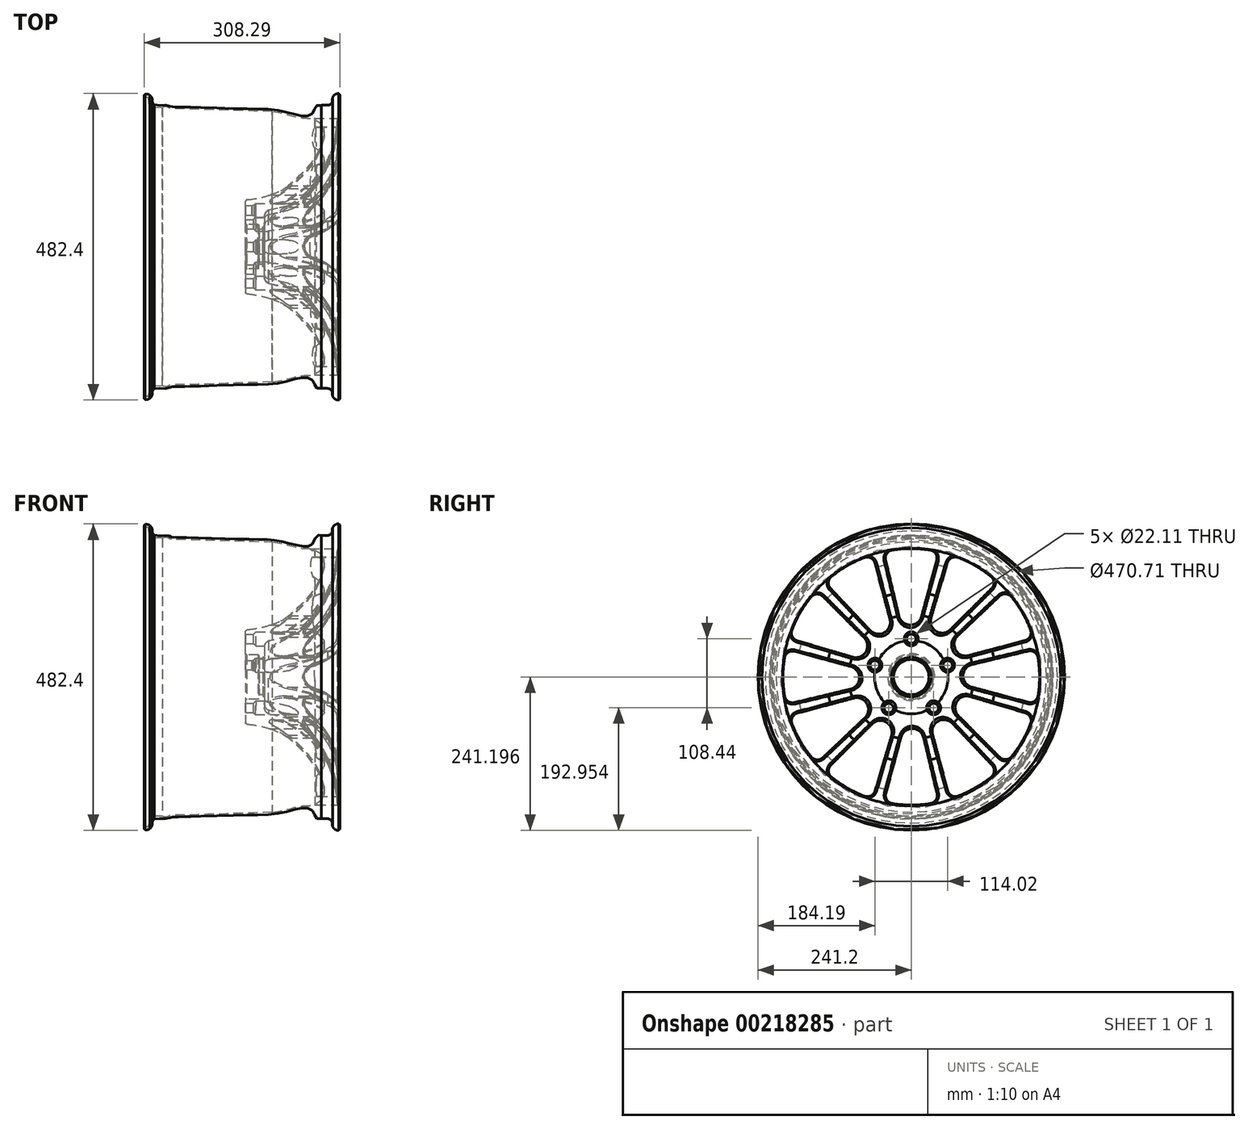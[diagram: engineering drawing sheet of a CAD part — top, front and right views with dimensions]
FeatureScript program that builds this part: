
annotation { "Feature Type Name" : "Feature", "Feature Type Description" : "" }
export const myFeature = defineFeature(function(context is Context, id is Id, definition is map)
    precondition{}
    {
        {
            var Q0;
            Q0=qCreatedBy(makeId("Front.planeOp"),FACE);
            var sketch = newSketch(context, id + "F0", { "sketchPlane" : qUnion([Q0])});
            skLineSegment(sketch, "E0", {"start": v(-76.45, -36.51) * mm, "end": v(-76.45, -20.16) * mm});
            skLineSegment(sketch, "E1", {"start": v(-69.98, -9.89) * mm, "end": v(-37.23, -2.41) * mm});
            skArc(sketch, "E2", {"start": v(-69.98, -9.89) * mm, "mid": v(-74.7, -14.09) * mm, "end": v(-76.45, -20.16) * mm});
            skFitSpline(sketch, "E3", {"points": [v(-37.23, -2.41) * mm, v(-17.73, 6.45) * mm, v(2.3, 30.38) * mm], "startDerivative": vector(46.63, 15.97) * mm, "endDerivative": vector(34.44, 46.87) * mm});
            skFitSpline(sketch, "E4", {"points": [v(2.3, 30.38) * mm, v(23.11, 65.83) * mm], "startDerivative": vector(28.94, 36.21) * mm, "endDerivative": vector(17.75, 37.52) * mm});
            skFitSpline(sketch, "E5", {"points": [v(23.11, 65.83) * mm, v(40.09, 126.8) * mm, v(40.76, 134.95) * mm], "startDerivative": vector(48.73, 100.19) * mm, "endDerivative": vector(-0.18, 23.94) * mm});
            skFitSpline(sketch, "E6", {"points": [v(40.76, 134.95) * mm, v(40.76, 158.65) * mm, v(41.73, 167.17) * mm], "startDerivative": vector(2.63, 42.3) * mm, "endDerivative": vector(3.15, 18.57) * mm});
            skArc(sketch, "E7", {"start": v(41.73, 167.17) * mm, "mid": v(42.53, 170.69) * mm, "end": v(40.17, 173.42) * mm});
            skArc(sketch, "E8", {"start": v(40.17, 173.42) * mm, "mid": v(34.51, 171.85) * mm, "end": v(30.96, 167.17) * mm});
            skFitSpline(sketch, "E9", {"points": [v(30.96, 167.17) * mm, v(30.02, 160.2) * mm, v(25.65, 155.75) * mm, v(12.9, 154.85) * mm], "startDerivative": vector(-11.18, -23.98) * mm, "endDerivative": vector(-39.84, -5.43) * mm});
            skFitSpline(sketch, "E10", {"points": [v(12.9, 154.85) * mm, v(10.67, 155.98) * mm, v(5.92, 154.3) * mm, v(-2.23, 140.57) * mm, v(-9.2, 138.22) * mm, v(-18.92, 138.56) * mm, v(-41.3, 143.92) * mm, v(-63.75, 148.22) * mm, v(-89.43, 149.11) * mm, v(-144.26, 150.4) * mm, v(-204.89, 152.18) * mm, v(-223.48, 152.85) * mm, v(-225.49, 153.97) * mm, v(-228.56, 155.48) * mm, v(-236.43, 154.85) * mm, v(-249.44, 155.76) * mm], "startDerivative": vector(-71.66, 50.77) * mm, "endDerivative": vector(-216.1, 28.33) * mm});
            skArc(sketch, "E11", {"start": v(-252.9, 162.18) * mm, "mid": v(-252.1, 158.47) * mm, "end": v(-249.44, 155.76) * mm});
            skArc(sketch, "E12", {"start": v(-252.9, 162.18) * mm, "mid": v(-253.67, 167) * mm, "end": v(-256.75, 170.77) * mm});
            skArc(sketch, "E13", {"start": v(-256.75, 170.77) * mm, "mid": v(-260.2, 172.5) * mm, "end": v(-264.07, 172.45) * mm});
            skArc(sketch, "E14", {"start": v(-264.07, 172.45) * mm, "mid": v(-265.64, 170.02) * mm, "end": v(-264.07, 167.6) * mm});
            skLineSegment(sketch, "E15", {"start": v(-264.07, 167.6) * mm, "end": v(-260.33, 167.6) * mm});
            skArc(sketch, "E16", {"start": v(-258.37, 165.7) * mm, "mid": v(-258.96, 167.04) * mm, "end": v(-260.33, 167.6) * mm});
            skLineSegment(sketch, "E17", {"start": v(-258.37, 165.7) * mm, "end": v(-258.2, 160.06) * mm});
            skArc(sketch, "E18", {"start": v(-258.2, 160.06) * mm, "mid": v(-255.87, 154.31) * mm, "end": v(-250.33, 151.51) * mm});
            skLineSegment(sketch, "E19", {"start": v(-250.33, 151.51) * mm, "end": v(-237.32, 151.07) * mm});
            skFitSpline(sketch, "E20", {"points": [v(-237.32, 151.07) * mm, v(-230.51, 152.52) * mm, v(-225.15, 150.12) * mm, v(-217.28, 149.5) * mm, v(-64.03, 144.98) * mm], "startDerivative": vector(53.95, 20.8) * mm, "endDerivative": vector(330.22, -11.39) * mm});
            skFitSpline(sketch, "E21", {"points": [v(-64.03, 144.98) * mm, v(-23.16, 135.94) * mm, v(-8.6, 134.65) * mm, v(2.9, 134.04) * mm], "startDerivative": vector(115.17, -13.47) * mm, "endDerivative": vector(46.54, -2.62) * mm});
            skArc(sketch, "E22", {"start": v(17.48, 113.27) * mm, "mid": v(14.75, 126.85) * mm, "end": v(2.9, 134.04) * mm});
            skFitSpline(sketch, "E23", {"points": [v(17.48, 113.27) * mm, v(10.72, 91.33) * mm, v(-0.6, 70) * mm, v(-24.06, 43.1) * mm, v(-51.25, 21.26) * mm, v(-106.01, 6.13) * mm], "startDerivative": vector(-37.17, -135.72) * mm, "endDerivative": vector(-271.78, -21.35) * mm});
            skLineSegment(sketch, "E24", {"start": v(-76.45, -36.51) * mm, "end": v(-78.84, -36.51) * mm});
            skLineSegment(sketch, "E25", {"start": v(-78.84, -36.51) * mm, "end": v(-78.84, -40.03) * mm});
            skLineSegment(sketch, "E26", {"start": v(-78.84, -40.03) * mm, "end": v(-84.35, -40.03) * mm});
            skLineSegment(sketch, "E27", {"start": v(-84.35, -40.03) * mm, "end": v(-85.35, -38.77) * mm});
            skLineSegment(sketch, "E28", {"start": v(-85.35, -38.77) * mm, "end": v(-85.35, -33.52) * mm});
            skLineSegment(sketch, "E29", {"start": v(-85.35, -33.52) * mm, "end": v(-86.34, -32.73) * mm});
            skLineSegment(sketch, "E30", {"start": v(-86.34, -32.73) * mm, "end": v(-104.27, -32.73) * mm});
            skLineSegment(sketch, "E31", {"start": v(-104.27, -32.73) * mm, "end": v(-106.4, -30.93) * mm});
            skLineSegment(sketch, "E32", {"start": v(-106.01, 6.13) * mm, "end": v(-106.4, -30.93) * mm});
            skSolve(sketch);
        }
        {
            var Q0;
            Q0=makeQuery(id+"F0.imprint","IMPRINT",FACE,{"disambiguationData":[TD([[makeQuery(id+"F0.imprint","IMPRINT",EDGE,{"derivedFrom":sQuery(id+"F0.wireOp",EDGE,"E0")}),1.0]])]});
            var sketch = newSketch(context, id + "F1", { "sketchPlane" : qUnion([Q0])});
            skLineSegment(sketch, "E33", {"start": v(-312.86, -67.76) * mm, "end": v(77.27, -67.76) * mm, "construction": true});
            skSolve(sketch);
        }
        {
            var Q0;
            Q0=makeQuery(id+"F0.imprint","IMPRINT",FACE,{"disambiguationData":[TD([[makeQuery(id+"F0.imprint","IMPRINT",EDGE,{"derivedFrom":sQuery(id+"F0.wireOp",EDGE,"E0")}),1.0]])]});
            var Q1;
            Q1=sQuery(id+"F1.wireOp",EDGE,"E33");
            revolve(context, id + "F2", {"entities" : qUnion([Q0]), "axis" : qUnion([Q1]), "revolveType" : RevolveType.FULL});
        }
        {
            var Q0;
            Q0=qCreatedBy(makeId("Right.planeOp"),FACE);
            cPlane(context, id + "F3", {"entities" : qUnion([Q0]), "cplaneType" : CPlaneType.OFFSET, "offset" : 43.18 * mm, "width" : 152.4 * mm, "height" : 152.4 * mm});
        }
        {
            var Q0;
            Q0=qCreatedBy(id+"F3.planeOp",FACE);
            var sketch = newSketch(context, id + "F4", { "sketchPlane" : qUnion([Q0])});
            skArc(sketch, "E34", {"start": v(43.5, 129.39) * mm, "mid": v(0, 134.5) * mm, "end": v(-43.5, 129.39) * mm});
            skArc(sketch, "E35.0", {"start": v(16.48, 28.98) * mm, "mid": v(-1.49, 30.6) * mm, "end": v(-19.39, 28.34) * mm});
            skLineSegment(sketch, "E36", {"start": v(43.5, 129.39) * mm, "end": v(16.48, 28.98) * mm});
            skLineSegment(sketch, "E37", {"start": v(-43.5, 129.39) * mm, "end": v(-19.39, 28.34) * mm});
            skArc(sketch, "E38.1.0", {"start": v(-33.87, 24.32) * mm, "mid": v(-50.25, 16.74) * mm, "end": v(-64.61, 5.83) * mm});
            skLineSegment(sketch, "E38.1.1", {"start": v(-60.68, 124.78) * mm, "end": v(-33.87, 24.32) * mm});
            skLineSegment(sketch, "E38.1.2", {"start": v(-136.02, 81.29) * mm, "end": v(-64.61, 5.83) * mm});
            skArc(sketch, "E38.1.3", {"start": v(-60.68, 124.78) * mm, "mid": v(-100.9, 107.47) * mm, "end": v(-136.02, 81.29) * mm});
            skArc(sketch, "E38.2.0", {"start": v(-75.15, -4.9) * mm, "mid": v(-85.54, -19.64) * mm, "end": v(-92.53, -36.28) * mm});
            skLineSegment(sketch, "E38.2.1", {"start": v(-148.6, 68.7) * mm, "end": v(-75.15, -4.9) * mm});
            skLineSegment(sketch, "E38.2.2", {"start": v(-192.1, -6.63) * mm, "end": v(-92.53, -36.28) * mm});
            skArc(sketch, "E38.2.3", {"start": v(-148.6, 68.7) * mm, "mid": v(-174.78, 33.6) * mm, "end": v(-192.1, -6.63) * mm});
            skArc(sketch, "E38.3.0", {"start": v(-96.29, -50.83) * mm, "mid": v(-97.92, -68.8) * mm, "end": v(-95.65, -86.7) * mm});
            skLineSegment(sketch, "E38.3.1", {"start": v(-196.7, -23.81) * mm, "end": v(-96.29, -50.83) * mm});
            skLineSegment(sketch, "E38.3.2", {"start": v(-196.7, -110.8) * mm, "end": v(-95.65, -86.7) * mm});
            skArc(sketch, "E38.3.3", {"start": v(-196.7, -23.81) * mm, "mid": v(-201.81, -67.3) * mm, "end": v(-196.7, -110.8) * mm});
            skArc(sketch, "E38.4.0", {"start": v(-91.63, -101.18) * mm, "mid": v(-84.05, -117.56) * mm, "end": v(-73.14, -131.92) * mm});
            skLineSegment(sketch, "E38.4.1", {"start": v(-192.1, -128) * mm, "end": v(-91.63, -101.18) * mm});
            skLineSegment(sketch, "E38.4.2", {"start": v(-148.6, -203.33) * mm, "end": v(-73.14, -131.92) * mm});
            skArc(sketch, "E38.4.3", {"start": v(-192.1, -128) * mm, "mid": v(-174.78, -168.22) * mm, "end": v(-148.6, -203.33) * mm});
            skArc(sketch, "E38.5.0", {"start": v(-62.41, -142.46) * mm, "mid": v(-47.67, -152.85) * mm, "end": v(-31.03, -159.84) * mm});
            skLineSegment(sketch, "E38.5.1", {"start": v(-136.02, -215.9) * mm, "end": v(-62.41, -142.46) * mm});
            skLineSegment(sketch, "E38.5.2", {"start": v(-60.68, -259.4) * mm, "end": v(-31.03, -159.84) * mm});
            skArc(sketch, "E38.5.3", {"start": v(-136.02, -215.9) * mm, "mid": v(-100.9, -242.09) * mm, "end": v(-60.68, -259.4) * mm});
            skArc(sketch, "E38.6.0", {"start": v(-16.48, -163.6) * mm, "mid": v(1.49, -165.23) * mm, "end": v(19.39, -162.96) * mm});
            skLineSegment(sketch, "E38.6.1", {"start": v(-43.5, -264) * mm, "end": v(-16.48, -163.6) * mm});
            skLineSegment(sketch, "E38.6.2", {"start": v(43.5, -264) * mm, "end": v(19.39, -162.96) * mm});
            skArc(sketch, "E38.6.3", {"start": v(-43.5, -264) * mm, "mid": v(0, -269.12) * mm, "end": v(43.5, -264) * mm});
            skArc(sketch, "E38.7.0", {"start": v(33.87, -158.94) * mm, "mid": v(50.25, -151.36) * mm, "end": v(64.61, -140.45) * mm});
            skLineSegment(sketch, "E38.7.1", {"start": v(60.68, -259.4) * mm, "end": v(33.87, -158.94) * mm});
            skLineSegment(sketch, "E38.7.2", {"start": v(136.02, -215.9) * mm, "end": v(64.61, -140.45) * mm});
            skArc(sketch, "E38.7.3", {"start": v(60.68, -259.4) * mm, "mid": v(100.9, -242.09) * mm, "end": v(136.02, -215.9) * mm});
            skArc(sketch, "E38.8.0", {"start": v(75.15, -129.72) * mm, "mid": v(85.54, -114.98) * mm, "end": v(92.53, -98.34) * mm});
            skLineSegment(sketch, "E38.8.1", {"start": v(148.6, -203.33) * mm, "end": v(75.15, -129.72) * mm});
            skLineSegment(sketch, "E38.8.2", {"start": v(192.1, -128) * mm, "end": v(92.53, -98.34) * mm});
            skArc(sketch, "E38.8.3", {"start": v(148.6, -203.33) * mm, "mid": v(174.78, -168.22) * mm, "end": v(192.1, -128) * mm});
            skArc(sketch, "E38.9.0", {"start": v(96.29, -83.79) * mm, "mid": v(97.92, -65.82) * mm, "end": v(95.65, -47.92) * mm});
            skLineSegment(sketch, "E38.9.1", {"start": v(196.7, -110.8) * mm, "end": v(96.29, -83.79) * mm});
            skLineSegment(sketch, "E38.9.2", {"start": v(196.7, -23.81) * mm, "end": v(95.65, -47.92) * mm});
            skArc(sketch, "E38.9.3", {"start": v(196.7, -110.8) * mm, "mid": v(201.81, -67.31) * mm, "end": v(196.7, -23.81) * mm});
            skArc(sketch, "E38.10.0", {"start": v(91.63, -33.44) * mm, "mid": v(84.05, -17.06) * mm, "end": v(73.14, -2.7) * mm});
            skLineSegment(sketch, "E38.10.1", {"start": v(192.1, -6.63) * mm, "end": v(91.63, -33.44) * mm});
            skLineSegment(sketch, "E38.10.2", {"start": v(148.6, 68.7) * mm, "end": v(73.14, -2.7) * mm});
            skArc(sketch, "E38.10.3", {"start": v(192.1, -6.63) * mm, "mid": v(174.78, 33.6) * mm, "end": v(148.6, 68.7) * mm});
            skPoint(sketch, "E38.center", {"position": v(0, -67.3) * mm});
            skArc(sketch, "E39.1.11.0", {"start": v(62.41, 7.84) * mm, "mid": v(47.67, 18.23) * mm, "end": v(31.03, 25.22) * mm});
            skLineSegment(sketch, "E39.4.11.0", {"start": v(136.02, 81.29) * mm, "end": v(62.41, 7.84) * mm});
            skLineSegment(sketch, "E39.7.11.0", {"start": v(60.68, 124.78) * mm, "end": v(31.03, 25.22) * mm});
            skArc(sketch, "E39.10.11.0", {"start": v(136.02, 81.29) * mm, "mid": v(100.9, 107.47) * mm, "end": v(60.68, 124.78) * mm});
            skArc(sketch, "E40", {"start": v(-19.39, 28.34) * mm, "mid": v(-1.2, 14.24) * mm, "end": v(16.48, 28.98) * mm});
            skArc(sketch, "E41.1.0", {"start": v(-64.61, 5.83) * mm, "mid": v(-41.81, 2.71) * mm, "end": v(-33.87, 24.32) * mm});
            skArc(sketch, "E41.2.0", {"start": v(-92.53, -36.28) * mm, "mid": v(-71.22, -27.57) * mm, "end": v(-75.15, -4.9) * mm});
            skArc(sketch, "E41.3.0", {"start": v(-95.65, -86.7) * mm, "mid": v(-81.55, -68.5) * mm, "end": v(-96.29, -50.83) * mm});
            skArc(sketch, "E41.4.0", {"start": v(-73.14, -131.92) * mm, "mid": v(-70.02, -109.12) * mm, "end": v(-91.63, -101.18) * mm});
            skArc(sketch, "E41.5.0", {"start": v(-31.03, -159.84) * mm, "mid": v(-39.74, -138.53) * mm, "end": v(-62.41, -142.46) * mm});
            skArc(sketch, "E41.6.0", {"start": v(19.39, -162.96) * mm, "mid": v(1.2, -148.86) * mm, "end": v(-16.48, -163.6) * mm});
            skArc(sketch, "E41.7.0", {"start": v(64.61, -140.45) * mm, "mid": v(41.81, -137.33) * mm, "end": v(33.87, -158.94) * mm});
            skArc(sketch, "E41.8.0", {"start": v(92.53, -98.34) * mm, "mid": v(71.22, -107.05) * mm, "end": v(75.15, -129.72) * mm});
            skArc(sketch, "E41.9.0", {"start": v(95.65, -47.92) * mm, "mid": v(81.55, -66.11) * mm, "end": v(96.29, -83.79) * mm});
            skArc(sketch, "E41.10.0", {"start": v(73.14, -2.7) * mm, "mid": v(70.02, -25.5) * mm, "end": v(91.63, -33.44) * mm});
            skArc(sketch, "E41.11.0", {"start": v(31.03, 25.22) * mm, "mid": v(39.74, 3.91) * mm, "end": v(62.41, 7.84) * mm});
            skSolve(sketch);
        }
        {
            var Q0;
            Q0=makeQuery(id+"F4.imprint","IMPRINT",FACE,{"disambiguationData":[TD([[makeQuery(id+"F4.imprint","IMPRINT",EDGE,{"derivedFrom":sQuery(id+"F4.wireOp",EDGE,"E38.3.0")}),-1.0]])]});
            var Q1;
            Q1=makeQuery(id+"F4.imprint","IMPRINT",FACE,{"disambiguationData":[TD([[makeQuery(id+"F4.imprint","IMPRINT",EDGE,{"derivedFrom":sQuery(id+"F4.wireOp",EDGE,"E38.2.0")}),-1.0]])]});
            var Q2;
            Q2=makeQuery(id+"F4.imprint","IMPRINT",FACE,{"disambiguationData":[TD([[makeQuery(id+"F4.imprint","IMPRINT",EDGE,{"derivedFrom":sQuery(id+"F4.wireOp",EDGE,"E38.1.0")}),-1.0]])]});
            var Q3;
            Q3=makeQuery(id+"F4.imprint","IMPRINT",FACE,{"disambiguationData":[TD([[makeQuery(id+"F4.imprint","IMPRINT",EDGE,{"derivedFrom":sQuery(id+"F4.wireOp",EDGE,"E34")}),1.0]])]});
            var Q4;
            Q4=makeQuery(id+"F4.imprint","IMPRINT",FACE,{"disambiguationData":[TD([[makeQuery(id+"F4.imprint","IMPRINT",EDGE,{"derivedFrom":sQuery(id+"F4.wireOp",EDGE,"E39.1.11.0")}),-1.0]])]});
            var Q5;
            Q5=makeQuery(id+"F4.imprint","IMPRINT",FACE,{"disambiguationData":[TD([[makeQuery(id+"F4.imprint","IMPRINT",EDGE,{"derivedFrom":sQuery(id+"F4.wireOp",EDGE,"E38.10.0")}),-1.0]])]});
            var Q6;
            Q6=makeQuery(id+"F4.imprint","IMPRINT",FACE,{"disambiguationData":[TD([[makeQuery(id+"F4.imprint","IMPRINT",EDGE,{"derivedFrom":sQuery(id+"F4.wireOp",EDGE,"E38.9.0")}),-1.0]])]});
            var Q7;
            Q7=makeQuery(id+"F4.imprint","IMPRINT",FACE,{"disambiguationData":[TD([[makeQuery(id+"F4.imprint","IMPRINT",EDGE,{"derivedFrom":sQuery(id+"F4.wireOp",EDGE,"E38.8.0")}),-1.0]])]});
            var Q8;
            Q8=makeQuery(id+"F4.imprint","IMPRINT",FACE,{"disambiguationData":[TD([[makeQuery(id+"F4.imprint","IMPRINT",EDGE,{"derivedFrom":sQuery(id+"F4.wireOp",EDGE,"E38.7.0")}),-1.0]])]});
            var Q9;
            Q9=makeQuery(id+"F4.imprint","IMPRINT",FACE,{"disambiguationData":[TD([[makeQuery(id+"F4.imprint","IMPRINT",EDGE,{"derivedFrom":sQuery(id+"F4.wireOp",EDGE,"E38.6.0")}),-1.0]])]});
            var Q10;
            Q10=makeQuery(id+"F4.imprint","IMPRINT",FACE,{"disambiguationData":[TD([[makeQuery(id+"F4.imprint","IMPRINT",EDGE,{"derivedFrom":sQuery(id+"F4.wireOp",EDGE,"E38.5.0")}),-1.0]])]});
            var Q11;
            Q11=makeQuery(id+"F4.imprint","IMPRINT",FACE,{"disambiguationData":[TD([[makeQuery(id+"F4.imprint","IMPRINT",EDGE,{"derivedFrom":sQuery(id+"F4.wireOp",EDGE,"E38.4.0")}),-1.0]])]});
            var Q12;
            Q12=makeQuery(id+"F4.imprint","IMPRINT",FACE,{"disambiguationData":[TD([[makeQuery(id+"F4.imprint","IMPRINT",EDGE,{"derivedFrom":sQuery(id+"F4.wireOp",EDGE,"E38.3.0")}),1.0]])]});
            var Q13;
            Q13=makeQuery(id+"F4.imprint","IMPRINT",FACE,{"disambiguationData":[TD([[makeQuery(id+"F4.imprint","IMPRINT",EDGE,{"derivedFrom":sQuery(id+"F4.wireOp",EDGE,"E38.2.0")}),1.0]])]});
            var Q14;
            Q14=makeQuery(id+"F4.imprint","IMPRINT",FACE,{"disambiguationData":[TD([[makeQuery(id+"F4.imprint","IMPRINT",EDGE,{"derivedFrom":sQuery(id+"F4.wireOp",EDGE,"E38.1.0")}),1.0]])]});
            var Q15;
            Q15=makeQuery(id+"F4.imprint","IMPRINT",FACE,{"disambiguationData":[TD([[makeQuery(id+"F4.imprint","IMPRINT",EDGE,{"derivedFrom":sQuery(id+"F4.wireOp",EDGE,"E35.0")}),1.0]])]});
            var Q16;
            Q16=makeQuery(id+"F4.imprint","IMPRINT",FACE,{"disambiguationData":[TD([[makeQuery(id+"F4.imprint","IMPRINT",EDGE,{"derivedFrom":sQuery(id+"F4.wireOp",EDGE,"E39.1.11.0")}),1.0]])]});
            var Q17;
            Q17=makeQuery(id+"F4.imprint","IMPRINT",FACE,{"disambiguationData":[TD([[makeQuery(id+"F4.imprint","IMPRINT",EDGE,{"derivedFrom":sQuery(id+"F4.wireOp",EDGE,"E38.9.0")}),1.0]])]});
            var Q18;
            Q18=makeQuery(id+"F4.imprint","IMPRINT",FACE,{"disambiguationData":[TD([[makeQuery(id+"F4.imprint","IMPRINT",EDGE,{"derivedFrom":sQuery(id+"F4.wireOp",EDGE,"E38.8.0")}),1.0]])]});
            var Q19;
            Q19=makeQuery(id+"F4.imprint","IMPRINT",FACE,{"disambiguationData":[TD([[makeQuery(id+"F4.imprint","IMPRINT",EDGE,{"derivedFrom":sQuery(id+"F4.wireOp",EDGE,"E38.7.0")}),1.0]])]});
            var Q20;
            Q20=makeQuery(id+"F4.imprint","IMPRINT",FACE,{"disambiguationData":[TD([[makeQuery(id+"F4.imprint","IMPRINT",EDGE,{"derivedFrom":sQuery(id+"F4.wireOp",EDGE,"E38.6.0")}),1.0]])]});
            var Q21;
            Q21=makeQuery(id+"F4.imprint","IMPRINT",FACE,{"disambiguationData":[TD([[makeQuery(id+"F4.imprint","IMPRINT",EDGE,{"derivedFrom":sQuery(id+"F4.wireOp",EDGE,"E38.5.0")}),1.0]])]});
            var Q22;
            Q22=makeQuery(id+"F4.imprint","IMPRINT",FACE,{"disambiguationData":[TD([[makeQuery(id+"F4.imprint","IMPRINT",EDGE,{"derivedFrom":sQuery(id+"F4.wireOp",EDGE,"E38.4.0")}),1.0]])]});
            var Q23;
            Q23=makeQuery(id+"F4.imprint","IMPRINT",FACE,{"disambiguationData":[TD([[makeQuery(id+"F4.imprint","IMPRINT",EDGE,{"derivedFrom":sQuery(id+"F4.wireOp",EDGE,"E38.10.0")}),1.0]])]});
            extrude(context, id + "F5", {"entities" : qUnion([Q0, Q1, Q2, Q3, Q4, Q5, Q6, Q7, Q8, Q9, Q10, Q11, Q12, Q13, Q14, Q15, Q16, Q17, Q18, Q19, Q20, Q21, Q22, Q23]), "operationType" : NewBodyOperationType.REMOVE, "oppositeDirection" : true, "depth" : 152.4 * mm});
        }
        {
            var Q0;
            Q0=makeQuery(id+"F5.boolean.opBoolean","COPY",EDGE,{"derivedFrom":makeQuery(id+"F5.opExtrude","SWEPT_EDGE",EDGE,{"disambiguationData":[OSD([sQuery(id+"F4.wireOp",EDGE,"E38.1.2"),sQuery(id+"F4.wireOp",EDGE,"E38.1.3")])]})});
            var Q1;
            Q1=makeQuery(id+"F5.boolean.opBoolean","COPY",EDGE,{"derivedFrom":makeQuery(id+"F5.opExtrude","SWEPT_EDGE",EDGE,{"disambiguationData":[OSD([sQuery(id+"F4.wireOp",EDGE,"E38.2.1"),sQuery(id+"F4.wireOp",EDGE,"E38.2.3")])]})});
            var Q2;
            Q2=makeQuery(id+"F5.boolean.opBoolean","COPY",EDGE,{"derivedFrom":makeQuery(id+"F5.opExtrude","SWEPT_EDGE",EDGE,{"disambiguationData":[OSD([sQuery(id+"F4.wireOp",EDGE,"E38.1.1"),sQuery(id+"F4.wireOp",EDGE,"E38.1.3")])]})});
            var Q3;
            Q3=makeQuery(id+"F5.boolean.opBoolean","COPY",EDGE,{"derivedFrom":makeQuery(id+"F5.opExtrude","SWEPT_EDGE",EDGE,{"disambiguationData":[OSD([sQuery(id+"F4.wireOp",EDGE,"E34"),sQuery(id+"F4.wireOp",EDGE,"E37")])]})});
            var Q4;
            Q4=makeQuery(id+"F5.boolean.opBoolean","COPY",EDGE,{"derivedFrom":makeQuery(id+"F5.opExtrude","SWEPT_EDGE",EDGE,{"disambiguationData":[OSD([sQuery(id+"F4.wireOp",EDGE,"E34"),sQuery(id+"F4.wireOp",EDGE,"E36")])]})});
            var Q5;
            Q5=makeQuery(id+"F5.boolean.opBoolean","COPY",EDGE,{"derivedFrom":makeQuery(id+"F5.opExtrude","SWEPT_EDGE",EDGE,{"disambiguationData":[OSD([sQuery(id+"F4.wireOp",EDGE,"E39.7.11.0"),sQuery(id+"F4.wireOp",EDGE,"E39.10.11.0")])]})});
            var Q6;
            Q6=makeQuery(id+"F5.boolean.opBoolean","COPY",EDGE,{"derivedFrom":makeQuery(id+"F5.opExtrude","SWEPT_EDGE",EDGE,{"disambiguationData":[OSD([sQuery(id+"F4.wireOp",EDGE,"E38.2.2"),sQuery(id+"F4.wireOp",EDGE,"E38.2.3")])]})});
            var Q7;
            Q7=makeQuery(id+"F5.boolean.opBoolean","COPY",EDGE,{"derivedFrom":makeQuery(id+"F5.opExtrude","SWEPT_EDGE",EDGE,{"disambiguationData":[OSD([sQuery(id+"F4.wireOp",EDGE,"E38.3.1"),sQuery(id+"F4.wireOp",EDGE,"E38.3.3")])]})});
            var Q8;
            Q8=makeQuery(id+"F5.boolean.opBoolean","COPY",EDGE,{"derivedFrom":makeQuery(id+"F5.opExtrude","SWEPT_EDGE",EDGE,{"disambiguationData":[OSD([sQuery(id+"F4.wireOp",EDGE,"E38.3.2"),sQuery(id+"F4.wireOp",EDGE,"E38.3.3")])]})});
            var Q9;
            Q9=makeQuery(id+"F5.boolean.opBoolean","COPY",EDGE,{"derivedFrom":makeQuery(id+"F5.opExtrude","SWEPT_EDGE",EDGE,{"disambiguationData":[OSD([sQuery(id+"F4.wireOp",EDGE,"E38.4.1"),sQuery(id+"F4.wireOp",EDGE,"E38.4.3")])]})});
            var Q10;
            Q10=makeQuery(id+"F5.boolean.opBoolean","COPY",EDGE,{"derivedFrom":makeQuery(id+"F5.opExtrude","SWEPT_EDGE",EDGE,{"disambiguationData":[OSD([sQuery(id+"F4.wireOp",EDGE,"E38.4.2"),sQuery(id+"F4.wireOp",EDGE,"E38.4.3")])]})});
            var Q11;
            Q11=makeQuery(id+"F5.boolean.opBoolean","COPY",EDGE,{"derivedFrom":makeQuery(id+"F5.opExtrude","SWEPT_EDGE",EDGE,{"disambiguationData":[OSD([sQuery(id+"F4.wireOp",EDGE,"E38.5.1"),sQuery(id+"F4.wireOp",EDGE,"E38.5.3")])]})});
            var Q12;
            Q12=makeQuery(id+"F5.boolean.opBoolean","COPY",EDGE,{"derivedFrom":makeQuery(id+"F5.opExtrude","SWEPT_EDGE",EDGE,{"disambiguationData":[OSD([sQuery(id+"F4.wireOp",EDGE,"E38.5.2"),sQuery(id+"F4.wireOp",EDGE,"E38.5.3")])]})});
            var Q13;
            Q13=makeQuery(id+"F5.boolean.opBoolean","COPY",EDGE,{"derivedFrom":makeQuery(id+"F5.opExtrude","SWEPT_EDGE",EDGE,{"disambiguationData":[OSD([sQuery(id+"F4.wireOp",EDGE,"E38.6.1"),sQuery(id+"F4.wireOp",EDGE,"E38.6.3")])]})});
            var Q14;
            Q14=makeQuery(id+"F5.boolean.opBoolean","COPY",EDGE,{"derivedFrom":makeQuery(id+"F5.opExtrude","SWEPT_EDGE",EDGE,{"disambiguationData":[OSD([sQuery(id+"F4.wireOp",EDGE,"E38.6.2"),sQuery(id+"F4.wireOp",EDGE,"E38.6.3")])]})});
            var Q15;
            Q15=makeQuery(id+"F5.boolean.opBoolean","COPY",EDGE,{"derivedFrom":makeQuery(id+"F5.opExtrude","SWEPT_EDGE",EDGE,{"disambiguationData":[OSD([sQuery(id+"F4.wireOp",EDGE,"E38.7.1"),sQuery(id+"F4.wireOp",EDGE,"E38.7.3")])]})});
            var Q16;
            Q16=makeQuery(id+"F5.boolean.opBoolean","COPY",EDGE,{"derivedFrom":makeQuery(id+"F5.opExtrude","SWEPT_EDGE",EDGE,{"disambiguationData":[OSD([sQuery(id+"F4.wireOp",EDGE,"E38.7.2"),sQuery(id+"F4.wireOp",EDGE,"E38.7.3")])]})});
            var Q17;
            Q17=makeQuery(id+"F5.boolean.opBoolean","COPY",EDGE,{"derivedFrom":makeQuery(id+"F5.opExtrude","SWEPT_EDGE",EDGE,{"disambiguationData":[OSD([sQuery(id+"F4.wireOp",EDGE,"E38.8.1"),sQuery(id+"F4.wireOp",EDGE,"E38.8.3")])]})});
            var Q18;
            Q18=makeQuery(id+"F5.boolean.opBoolean","COPY",EDGE,{"derivedFrom":makeQuery(id+"F5.opExtrude","SWEPT_EDGE",EDGE,{"disambiguationData":[OSD([sQuery(id+"F4.wireOp",EDGE,"E38.8.2"),sQuery(id+"F4.wireOp",EDGE,"E38.8.3")])]})});
            var Q19;
            Q19=makeQuery(id+"F5.boolean.opBoolean","COPY",EDGE,{"derivedFrom":makeQuery(id+"F5.opExtrude","SWEPT_EDGE",EDGE,{"disambiguationData":[OSD([sQuery(id+"F4.wireOp",EDGE,"E38.9.1"),sQuery(id+"F4.wireOp",EDGE,"E38.9.3")])]})});
            var Q20;
            Q20=makeQuery(id+"F5.boolean.opBoolean","COPY",EDGE,{"derivedFrom":makeQuery(id+"F5.opExtrude","SWEPT_EDGE",EDGE,{"disambiguationData":[OSD([sQuery(id+"F4.wireOp",EDGE,"E38.9.2"),sQuery(id+"F4.wireOp",EDGE,"E38.9.3")])]})});
            var Q21;
            Q21=makeQuery(id+"F5.boolean.opBoolean","COPY",EDGE,{"derivedFrom":makeQuery(id+"F5.opExtrude","SWEPT_EDGE",EDGE,{"disambiguationData":[OSD([sQuery(id+"F4.wireOp",EDGE,"E38.10.1"),sQuery(id+"F4.wireOp",EDGE,"E38.10.3")])]})});
            var Q22;
            Q22=makeQuery(id+"F5.boolean.opBoolean","COPY",EDGE,{"derivedFrom":makeQuery(id+"F5.opExtrude","SWEPT_EDGE",EDGE,{"disambiguationData":[OSD([sQuery(id+"F4.wireOp",EDGE,"E38.10.2"),sQuery(id+"F4.wireOp",EDGE,"E38.10.3")])]})});
            var Q23;
            Q23=makeQuery(id+"F5.boolean.opBoolean","COPY",EDGE,{"derivedFrom":makeQuery(id+"F5.opExtrude","SWEPT_EDGE",EDGE,{"disambiguationData":[OSD([sQuery(id+"F4.wireOp",EDGE,"E39.4.11.0"),sQuery(id+"F4.wireOp",EDGE,"E39.10.11.0")])]})});
            fillet(context, id + "F6", {"entities" : qUnion([Q0, Q1, Q2, Q3, Q4, Q5, Q6, Q7, Q8, Q9, Q10, Q11, Q12, Q13, Q14, Q15, Q16, Q17, Q18, Q19, Q20, Q21, Q22, Q23]), "radius" : 12.7 * mm, "tangentPropagation" : true, "allowEdgeOverflow" : false});
        }
        {
            var Q0;
            Q0=makeQuery(id+"F2.opRevolve","SWEPT_EDGE",EDGE,{"disambiguationData":[OSD([sQuery(id+"F0.wireOp",EDGE,"E1"),sQuery(id+"F0.wireOp",EDGE,"E3")])]});
            fillet(context, id + "F7", {"entities" : qUnion([Q0]), "radius" : 25.4 * mm, "tangentPropagation" : true, "allowEdgeOverflow" : false});
        }
        {
            var Q0;
            Q0=makeQuery(id+"F2.opRevolve","SWEPT_EDGE",EDGE,{"disambiguationData":[OSD([sQuery(id+"F0.wireOp",EDGE,"E23"),sQuery(id+"F0.wireOp",EDGE,"E32")])]});
            fillet(context, id + "F8", {"entities" : qUnion([Q0]), "radius" : 2.54 * mm, "tangentPropagation" : true, "allowEdgeOverflow" : false});
        }
        {
            var Q0;
            Q0=makeQuery(id+"F5.boolean.opBoolean","INTERSECT",EDGE,{"derivedFrom":[makeQuery(id+"F2.opRevolve","SWEPT_FACE",FACE,{"disambiguationData":[OSD([sQuery(id+"F0.wireOp",EDGE,"E5")])]}),makeQuery(id+"F5.opExtrude","SWEPT_FACE",FACE,{"disambiguationData":[OSD([sQuery(id+"F4.wireOp",EDGE,"E38.9.2")])]})]});
            var Q1;
            Q1=makeQuery(id+"F5.boolean.opBoolean","INTERSECT",EDGE,{"derivedFrom":[makeQuery(id+"F2.opRevolve","SWEPT_FACE",FACE,{"disambiguationData":[OSD([sQuery(id+"F0.wireOp",EDGE,"E5")])]}),makeQuery(id+"F5.opExtrude","SWEPT_FACE",FACE,{"disambiguationData":[OSD([sQuery(id+"F4.wireOp",EDGE,"E38.10.2")])]})]});
            var Q2;
            Q2=makeQuery(id+"F5.boolean.opBoolean","INTERSECT",EDGE,{"derivedFrom":[makeQuery(id+"F2.opRevolve","SWEPT_FACE",FACE,{"disambiguationData":[OSD([sQuery(id+"F0.wireOp",EDGE,"E5")])]}),makeQuery(id+"F5.opExtrude","SWEPT_FACE",FACE,{"disambiguationData":[OSD([sQuery(id+"F4.wireOp",EDGE,"E39.7.11.0")])]})]});
            var Q3;
            Q3=makeQuery(id+"F5.boolean.opBoolean","INTERSECT",EDGE,{"derivedFrom":[makeQuery(id+"F2.opRevolve","SWEPT_FACE",FACE,{"disambiguationData":[OSD([sQuery(id+"F0.wireOp",EDGE,"E5")])]}),makeQuery(id+"F5.opExtrude","SWEPT_FACE",FACE,{"disambiguationData":[OSD([sQuery(id+"F4.wireOp",EDGE,"E37")])]})]});
            var Q4;
            Q4=makeQuery(id+"F5.boolean.opBoolean","INTERSECT",EDGE,{"derivedFrom":[makeQuery(id+"F2.opRevolve","SWEPT_FACE",FACE,{"disambiguationData":[OSD([sQuery(id+"F0.wireOp",EDGE,"E5")])]}),makeQuery(id+"F5.opExtrude","SWEPT_FACE",FACE,{"disambiguationData":[OSD([sQuery(id+"F4.wireOp",EDGE,"E38.1.2")])]})]});
            var Q5;
            Q5=makeQuery(id+"F5.boolean.opBoolean","INTERSECT",EDGE,{"derivedFrom":[makeQuery(id+"F2.opRevolve","SWEPT_FACE",FACE,{"disambiguationData":[OSD([sQuery(id+"F0.wireOp",EDGE,"E5")])]}),makeQuery(id+"F5.opExtrude","SWEPT_FACE",FACE,{"disambiguationData":[OSD([sQuery(id+"F4.wireOp",EDGE,"E38.2.2")])]})]});
            var Q6;
            Q6=makeQuery(id+"F5.boolean.opBoolean","INTERSECT",EDGE,{"derivedFrom":[makeQuery(id+"F2.opRevolve","SWEPT_FACE",FACE,{"disambiguationData":[OSD([sQuery(id+"F0.wireOp",EDGE,"E5")])]}),makeQuery(id+"F5.opExtrude","SWEPT_FACE",FACE,{"disambiguationData":[OSD([sQuery(id+"F4.wireOp",EDGE,"E38.3.2")])]})]});
            var Q7;
            Q7=makeQuery(id+"F5.boolean.opBoolean","INTERSECT",EDGE,{"derivedFrom":[makeQuery(id+"F2.opRevolve","SWEPT_FACE",FACE,{"disambiguationData":[OSD([sQuery(id+"F0.wireOp",EDGE,"E5")])]}),makeQuery(id+"F5.opExtrude","SWEPT_FACE",FACE,{"disambiguationData":[OSD([sQuery(id+"F4.wireOp",EDGE,"E38.4.2")])]})]});
            var Q8;
            Q8=makeQuery(id+"F5.boolean.opBoolean","INTERSECT",EDGE,{"derivedFrom":[makeQuery(id+"F2.opRevolve","SWEPT_FACE",FACE,{"disambiguationData":[OSD([sQuery(id+"F0.wireOp",EDGE,"E5")])]}),makeQuery(id+"F5.opExtrude","SWEPT_FACE",FACE,{"disambiguationData":[OSD([sQuery(id+"F4.wireOp",EDGE,"E38.5.2")])]})]});
            var Q9;
            Q9=makeQuery(id+"F5.boolean.opBoolean","INTERSECT",EDGE,{"derivedFrom":[makeQuery(id+"F2.opRevolve","SWEPT_FACE",FACE,{"disambiguationData":[OSD([sQuery(id+"F0.wireOp",EDGE,"E5")])]}),makeQuery(id+"F5.opExtrude","SWEPT_FACE",FACE,{"disambiguationData":[OSD([sQuery(id+"F4.wireOp",EDGE,"E38.6.2")])]})]});
            var Q10;
            Q10=makeQuery(id+"F5.boolean.opBoolean","INTERSECT",EDGE,{"derivedFrom":[makeQuery(id+"F2.opRevolve","SWEPT_FACE",FACE,{"disambiguationData":[OSD([sQuery(id+"F0.wireOp",EDGE,"E5")])]}),makeQuery(id+"F5.opExtrude","SWEPT_FACE",FACE,{"disambiguationData":[OSD([sQuery(id+"F4.wireOp",EDGE,"E38.7.2")])]})]});
            var Q11;
            Q11=makeQuery(id+"F5.boolean.opBoolean","INTERSECT",EDGE,{"derivedFrom":[makeQuery(id+"F2.opRevolve","SWEPT_FACE",FACE,{"disambiguationData":[OSD([sQuery(id+"F0.wireOp",EDGE,"E5")])]}),makeQuery(id+"F5.opExtrude","SWEPT_FACE",FACE,{"disambiguationData":[OSD([sQuery(id+"F4.wireOp",EDGE,"E38.8.2")])]})]});
            fillet(context, id + "F9", {"entities" : qUnion([Q0, Q1, Q2, Q3, Q4, Q5, Q6, Q7, Q8, Q9, Q10, Q11]), "radius" : 2.54 * mm, "tangentPropagation" : true, "allowEdgeOverflow" : false});
        }
        {
            var Q0;
            Q0=qCreatedBy(makeId("Right.planeOp"),FACE);
            var sketch = newSketch(context, id + "F10", { "sketchPlane" : qUnion([Q0])});
            skCircle(sketch, "E42", {"center": v(0, -67.5) * mm, "radius": 59.94 * mm, "construction": true});
            skCircle(sketch, "E43", {"center": v(0, -7.57) * mm, "radius": 6.74 * mm});
            skCircle(sketch, "E44.1.1", {"center": v(-57.01, -48.99) * mm, "radius": 6.74 * mm});
            skCircle(sketch, "E44.2.1", {"center": v(-35.23, -116) * mm, "radius": 6.74 * mm});
            skCircle(sketch, "E44.3.1", {"center": v(35.23, -116) * mm, "radius": 6.74 * mm});
            skCircle(sketch, "E44.4.1", {"center": v(57.01, -48.99) * mm, "radius": 6.74 * mm});
            skCircle(sketch, "E45.0", {"center": v(0, -7.57) * mm, "radius": 11.05 * mm});
            skCircle(sketch, "E46.1.0", {"center": v(-57.01, -48.99) * mm, "radius": 11.05 * mm});
            skCircle(sketch, "E46.2.0", {"center": v(-35.23, -116) * mm, "radius": 11.05 * mm});
            skCircle(sketch, "E46.3.0", {"center": v(35.23, -116) * mm, "radius": 11.05 * mm});
            skCircle(sketch, "E46.4.0", {"center": v(57.01, -48.99) * mm, "radius": 11.05 * mm});
            skSolve(sketch);
        }
        {
            var Q0;
            Q0=makeQuery(id+"F10.imprint","IMPRINT",FACE,{"disambiguationData":[TD([[makeQuery(id+"F10.imprint","IMPRINT",EDGE,{"derivedFrom":sQuery(id+"F10.wireOp",EDGE,"E44.1.1")}),1.0]])]});
            var Q1;
            Q1=makeQuery(id+"F10.imprint","IMPRINT",FACE,{"disambiguationData":[TD([[makeQuery(id+"F10.imprint","IMPRINT",EDGE,{"derivedFrom":sQuery(id+"F10.wireOp",EDGE,"E43")}),1.0]])]});
            var Q2;
            Q2=makeQuery(id+"F10.imprint","IMPRINT",FACE,{"disambiguationData":[TD([[makeQuery(id+"F10.imprint","IMPRINT",EDGE,{"derivedFrom":sQuery(id+"F10.wireOp",EDGE,"E44.4.1")}),1.0]])]});
            var Q3;
            Q3=makeQuery(id+"F10.imprint","IMPRINT",FACE,{"disambiguationData":[TD([[makeQuery(id+"F10.imprint","IMPRINT",EDGE,{"derivedFrom":sQuery(id+"F10.wireOp",EDGE,"E44.3.1")}),1.0]])]});
            var Q4;
            Q4=makeQuery(id+"F10.imprint","IMPRINT",FACE,{"disambiguationData":[TD([[makeQuery(id+"F10.imprint","IMPRINT",EDGE,{"derivedFrom":sQuery(id+"F10.wireOp",EDGE,"E44.2.1")}),1.0]])]});
            var Q5;
            Q5=makeQuery(id+"F10.imprint","IMPRINT",FACE,{"disambiguationData":[TD([[makeQuery(id+"F10.imprint","IMPRINT",EDGE,{"derivedFrom":sQuery(id+"F10.wireOp",EDGE,"E44.1.1")}),-1.0]])]});
            var Q6;
            Q6=makeQuery(id+"F10.imprint","IMPRINT",FACE,{"disambiguationData":[TD([[makeQuery(id+"F10.imprint","IMPRINT",EDGE,{"derivedFrom":sQuery(id+"F10.wireOp",EDGE,"E43")}),-1.0]])]});
            var Q7;
            Q7=makeQuery(id+"F10.imprint","IMPRINT",FACE,{"disambiguationData":[TD([[makeQuery(id+"F10.imprint","IMPRINT",EDGE,{"derivedFrom":sQuery(id+"F10.wireOp",EDGE,"E44.4.1")}),-1.0]])]});
            var Q8;
            Q8=makeQuery(id+"F10.imprint","IMPRINT",FACE,{"disambiguationData":[TD([[makeQuery(id+"F10.imprint","IMPRINT",EDGE,{"derivedFrom":sQuery(id+"F10.wireOp",EDGE,"E44.3.1")}),-1.0]])]});
            var Q9;
            Q9=makeQuery(id+"F10.imprint","IMPRINT",FACE,{"disambiguationData":[TD([[makeQuery(id+"F10.imprint","IMPRINT",EDGE,{"derivedFrom":sQuery(id+"F10.wireOp",EDGE,"E44.2.1")}),-1.0]])]});
            var Q10;
            Q10=sQuery(id+"F10.wireOp",EDGE,"E43");
            var Q11;
            Q11=sQuery(id+"F10.wireOp",EDGE,"E44.4.1");
            var Q12;
            Q12=sQuery(id+"F10.wireOp",EDGE,"E44.3.1");
            var Q13;
            Q13=sQuery(id+"F10.wireOp",EDGE,"E44.2.1");
            var Q14;
            Q14=sQuery(id+"F10.wireOp",EDGE,"E44.1.1");
            extrude(context, id + "F11", {"entities" : qUnion([Q0, Q1, Q2, Q3, Q4, Q5, Q6, Q7, Q8, Q9]), "operationType" : NewBodyOperationType.REMOVE, "surfaceEntities" : qUnion([Q10, Q11, Q12, Q13, Q14]), "oppositeDirection" : true, "depth" : 88.9 * mm});
        }
        {
            var Q0;
            Q0=qCreatedBy(id+"F3.planeOp",FACE);
            var sketch = newSketch(context, id + "F12", { "sketchPlane" : qUnion([Q0])});
            skCircle(sketch, "E47", {"center": v(0, -7.54) * mm, "radius": 7.33 * mm});
            skCircle(sketch, "E48.1.0", {"center": v(-57.33, -49.2) * mm, "radius": 7.33 * mm});
            skCircle(sketch, "E48.2.0", {"center": v(-35.43, -116.58) * mm, "radius": 7.33 * mm});
            skCircle(sketch, "E48.3.0", {"center": v(35.43, -116.58) * mm, "radius": 7.33 * mm});
            skCircle(sketch, "E48.4.0", {"center": v(57.33, -49.2) * mm, "radius": 7.33 * mm});
            skPoint(sketch, "E48.center", {"position": v(0, -67.82) * mm});
            skSolve(sketch);
        }
        {
            var Q0;
            Q0 = qSketchRegion(id + "F12", true);
            extrude(context, id + "F13", {"entities" : qUnion([Q0]), "operationType" : NewBodyOperationType.REMOVE, "oppositeDirection" : true, "depth" : 152.4 * mm});
        }
        {
            var Q0;
            Q0=makeQuery(id+"F13.boolean.opBoolean","INTERSECT",EDGE,{"derivedFrom":[makeQuery(id+"F11.boolean.opBoolean","COPY",FACE,{"derivedFrom":makeQuery(id+"F11.opExtrude","CAP_FACE",FACE,{"disambiguationData":[OSD([sQuery(id+"F10.wireOp",EDGE,"E46.4.0")])],"isStart":false})}),makeQuery(id+"F13.opExtrude","SWEPT_FACE",FACE,{"disambiguationData":[OSD([sQuery(id+"F12.wireOp",EDGE,"E48.4.0")])]})]});
            chamfer(context, id + "F14", {"entities" : qUnion([Q0]), "width" : 5.08 * mm, "tangentPropagation" : true});
        }
        {
            var Q0;
            {var subQ0=makeQuery(id+"F13.opExtrude","SWEPT_FACE",FACE,{"disambiguationData":[OSD([sQuery(id+"F12.wireOp",EDGE,"E48.4.0")])]});Q0=makeQuery(id+"F14.opChamfer","BLEND_EDGE",EDGE,{"blendedFrom":[makeQuery(id+"F13.boolean.opBoolean","INTERSECT",EDGE,{"derivedFrom":[makeQuery(id+"F11.boolean.opBoolean","COPY",FACE,{"derivedFrom":makeQuery(id+"F11.opExtrude","CAP_FACE",FACE,{"disambiguationData":[OSD([sQuery(id+"F10.wireOp",EDGE,"E46.4.0")])],"isStart":false})}),subQ0]}),makeQuery(id+"F13.boolean.opBoolean","COPY",FACE,{"derivedFrom":subQ0})],"blendedInto":[makeQuery(id+"F13.boolean.opBoolean","COPY",FACE,{"derivedFrom":subQ0})]});}
            var Q1;
            Q1=makeQuery(id+"F13.boolean.opBoolean","INTERSECT",EDGE,{"derivedFrom":[makeQuery(id+"F11.boolean.opBoolean","COPY",FACE,{"derivedFrom":makeQuery(id+"F11.opExtrude","CAP_FACE",FACE,{"disambiguationData":[OSD([sQuery(id+"F10.wireOp",EDGE,"E45.0")])],"isStart":false})}),makeQuery(id+"F13.opExtrude","SWEPT_FACE",FACE,{"disambiguationData":[OSD([sQuery(id+"F12.wireOp",EDGE,"E47")])]})]});
            var Q2;
            Q2=makeQuery(id+"F13.boolean.opBoolean","INTERSECT",EDGE,{"derivedFrom":[makeQuery(id+"F11.boolean.opBoolean","COPY",FACE,{"derivedFrom":makeQuery(id+"F11.opExtrude","CAP_FACE",FACE,{"disambiguationData":[OSD([sQuery(id+"F10.wireOp",EDGE,"E46.1.0")])],"isStart":false})}),makeQuery(id+"F13.opExtrude","SWEPT_FACE",FACE,{"disambiguationData":[OSD([sQuery(id+"F12.wireOp",EDGE,"E48.1.0")])]})]});
            var Q3;
            Q3=makeQuery(id+"F13.boolean.opBoolean","INTERSECT",EDGE,{"derivedFrom":[makeQuery(id+"F11.boolean.opBoolean","COPY",FACE,{"derivedFrom":makeQuery(id+"F11.opExtrude","CAP_FACE",FACE,{"disambiguationData":[OSD([sQuery(id+"F10.wireOp",EDGE,"E46.2.0")])],"isStart":false})}),makeQuery(id+"F13.opExtrude","SWEPT_FACE",FACE,{"disambiguationData":[OSD([sQuery(id+"F12.wireOp",EDGE,"E48.2.0")])]})]});
            var Q4;
            Q4=makeQuery(id+"F13.boolean.opBoolean","INTERSECT",EDGE,{"derivedFrom":[makeQuery(id+"F11.boolean.opBoolean","COPY",FACE,{"derivedFrom":makeQuery(id+"F11.opExtrude","CAP_FACE",FACE,{"disambiguationData":[OSD([sQuery(id+"F10.wireOp",EDGE,"E46.3.0")])],"isStart":false})}),makeQuery(id+"F13.opExtrude","SWEPT_FACE",FACE,{"disambiguationData":[OSD([sQuery(id+"F12.wireOp",EDGE,"E48.3.0")])]})]});
            chamfer(context, id + "F15", {"entities" : qUnion([Q0, Q1, Q2, Q3, Q4]), "width" : 4.83 * mm, "tangentPropagation" : true});
        }
    });
